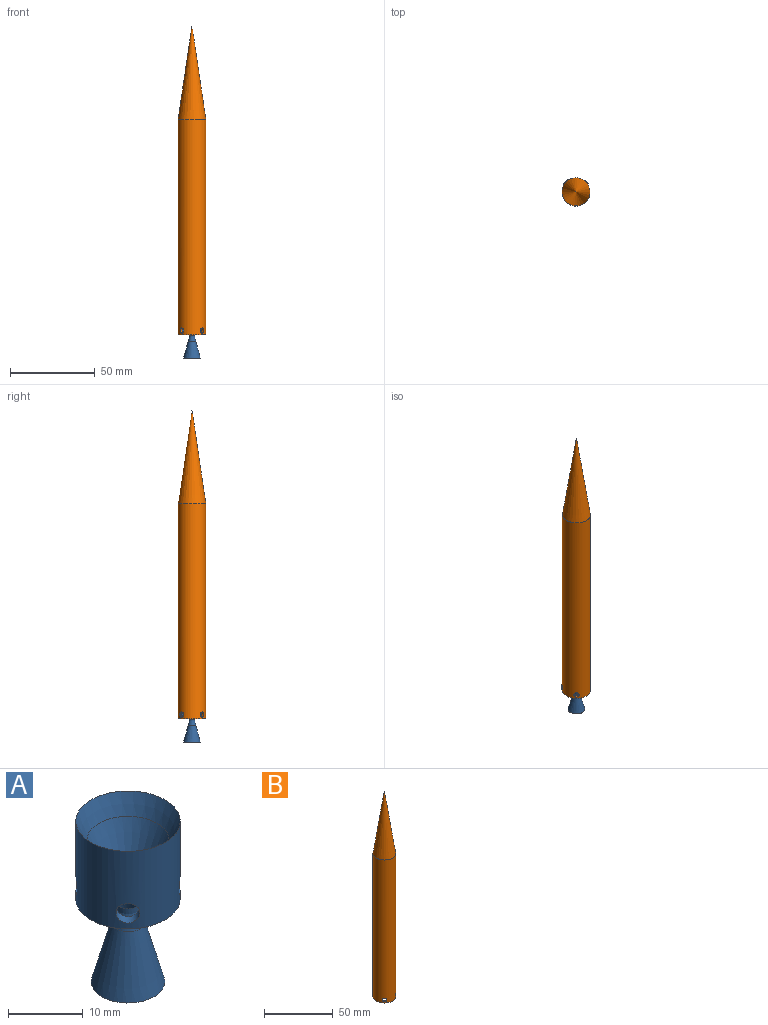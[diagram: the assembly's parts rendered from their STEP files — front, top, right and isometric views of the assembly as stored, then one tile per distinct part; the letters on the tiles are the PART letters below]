
ASSEMBLY  parts=2 mates=1
PART A: 15 faces, bbox 14x14x26.3 mm
  f0: cylinder r=6.99mm len=13.97mm, axis (0,0,-1), area 525.4mm2, adj f7,f8,f11,f12,f13,f14
  f1: cylinder r=5.48mm len=10.97mm, axis (0,0,-1), area 236.1mm2, adj f8,f9,f11,f12,f13,f14
  f2: cone r=2.27mm half-angle=15deg, axis (0,0,-1), area 229.1mm2, adj f3,f10
  f3: plane 9.82x9.82mm, normal (0,0,-1), area 18.1mm2, adj f2,f4
  f4: cone r=1.5mm half-angle=15deg, axis (0,0,-1), area 194.7mm2, adj f3,f5
  f5: revolved ~3.26x3.01mm, area 24.1mm2, adj f4,f6
  f6: cone r=5.48mm half-angle=24.8deg, axis (0,0,1), area 216.9mm2, adj f5,f7
  f7: cone r=6.99mm half-angle=25.9deg, axis (0,0,1), area 134.7mm2, adj f0,f6
  f8: plane 13.97x13.97mm, normal (0,0,-1), area 58.8mm2, adj f0,f1
  f9: cone r=5.48mm half-angle=24.8deg, axis (0,0,1), area 203.7mm2, adj f1,f10
  f10: revolved ~4.55x4.55mm, area 40.7mm2, adj f2,f9
  f11: cylinder r=1.59mm len=3.47mm, axis (-0.71,0.71,0), area 15.2mm2, adj f0,f1
  f12: cylinder r=1.59mm len=3.47mm, axis (0.71,-0.71,0), area 15.2mm2, adj f0,f1
  f13: cylinder r=1.59mm len=3.47mm, axis (0.71,0.71,0), area 15.2mm2, adj f0,f1
  f14: cylinder r=1.59mm len=3.47mm, axis (-0.71,-0.71,0), area 15.2mm2, adj f0,f1
PART B: 31 faces, bbox 16.5x16.5x182.5 mm
  f0: cylinder r=1.59mm len=1.33mm, axis (-0.71,-0.71,0), area 0mm2, adj f1,f16,f17
  f1: cylinder r=8.26mm len=127mm, axis (0,0,-1), area 6555.3mm2, adj f0,f3,f4,f6,f7,f12,f13,f18
  f2: cylinder r=6.99mm len=64.99mm, axis (0,0,-1), area 2820.4mm2, adj f4,f5,f6,f7,f8,f26
  f3: plane 16.52x16.52mm, normal (0,0,1), area 2.3mm2, adj f1,f27
  f4: plane 16.51x16.51mm, normal (0,0,-1), area 60.8mm2, adj f1,f2
  f5: cylinder r=1.59mm len=3.18mm, axis (0.71,-0.71,0), area 2.2mm2, adj f2,f20,f25
  f6: cylinder r=1.59mm len=3.18mm, axis (0.71,-0.71,0), area 12.7mm2, adj f1,f2
  f7: cylinder r=1.59mm len=3.18mm, axis (-0.71,-0.71,0), area 12.7mm2, adj f1,f2
  f8: cylinder r=1.59mm len=3.18mm, axis (-0.71,-0.71,0), area 2.4mm2, adj f2,f9,f15,f16,f17
  f9: cylinder r=1.59mm len=3.18mm, axis (-0.71,-0.71,0), area 0.1mm2, adj f8,f10,f16,f17
  f10: cylinder r=1.59mm len=3.18mm, axis (-0.71,-0.71,0), area 0.1mm2, adj f9,f11,f16,f17
  f11: cylinder r=1.59mm len=3.18mm, axis (-0.71,-0.71,0), area 0.1mm2, adj f10,f12,f16,f17
  f12: cylinder r=1.59mm len=3.18mm, axis (-0.71,-0.71,0), area 0mm2, adj f1,f11,f16,f17
  f13: cylinder r=1.59mm len=3.18mm, axis (-0.71,-0.71,0), area 3.9mm2, adj f1,f14,f16,f17
  f14: plane 0.2x0.2mm, normal (0,0,-1), area 0mm2, adj f13,f16,f17
  f15: plane 0.16x0.16mm, normal (0.53,-0.53,0.65), area 0mm2, adj f8,f16,f17
  f16: bspline ~3.67x3.23mm, area 13.4mm2, adj f0,f8,f9,f10,f11,f12,f13,f14
  f17: bspline ~3.67x3.23mm, area 13.3mm2, adj f0,f8,f9,f10,f11,f12,f13,f14
  f18: cylinder r=1.59mm len=1.9mm, axis (-0.71,-0.71,0), area 0mm2, adj f1,f16
  f19: plane 0.27x0.22mm, normal (0,0,-1), area 0mm2, adj f21,f22,f23,f24
  f20: plane 0.21x0.18mm, normal (0.53,0.53,0.65), area 0mm2, adj f5,f23,f24,f25
  f21: bspline ~3.17x2.32mm, area 0.7mm2, adj f19,f22,f23
  f22: cylinder r=1.59mm len=3.18mm, axis (0.71,-0.71,0), area 4.5mm2, adj f1,f19,f21
  f23: bspline ~3.53x3.15mm, area 13.2mm2, adj f19,f20,f21,f24
  f24: bspline ~3.53x3.15mm, area 13.1mm2, adj f19,f20,f23,f25
  f25: bspline ~3.6x2.52mm, area 0.7mm2, adj f5,f20,f24
  f26: plane 13.97x13.97mm, normal (0,0,-1), area 153.3mm2, adj f2
  f27: cone r=8.21mm half-angle=8.4deg, axis (0,0,-1), area 1446.6mm2, adj f3
  f28: plane 13.98x13.98mm, normal (0,0,-1), area 153.3mm2, adj f30
  f29: plane 13.97x13.97mm, normal (0,0,1), area 153.3mm2, adj f30
  f30: cylinder r=6.99mm len=59.47mm, axis (0,0,-1), area 2609.9mm2, adj f28,f29
PLACE A t=(-401.4,0,-0.05)mm
PLACE B t=(-401.4,0,-0.05)mm
MATE fastened A.f0 <-> B.f1  axis (0,0,-1) through (-401.4,0,-0.05)mm
